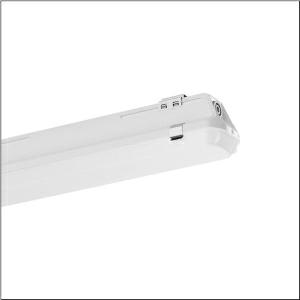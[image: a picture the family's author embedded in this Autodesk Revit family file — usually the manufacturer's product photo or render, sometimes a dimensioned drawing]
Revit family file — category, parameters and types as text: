
# Revit family: monsun_r__21_emergency_51fb107p487b3g_e760
name_source: partatom
category: Lighting Fixtures
units: mm (PartAtom-declared; Revit-internal decimal feet)

## family parameters
Cut with Voids When Loaded = No
Host = Face
Light Source = No
Part Type = Normal
Room Calculation Point = No
Round Connector Dimension = Use Diameter
Shared = No

## types (1)
- Monsun® 21 emergency (1 x LED, 8090 lm, 57.3 W, 4000K)
    Apparent Load = 57 VA
    CIE Flux Codes = 47 77 93 94 100
    Color Rendering = 80
    Color Temperature = 4000K
    Default Elevation = 1800 mm
    Description = Monsun® 21 emergency, damp-proof luminaire, chain hanger, primary optical cover: enclosure, of PMMA, light emission: direct distribution, primary light characteristic: symmetric, installation type: vertical mounting, horizontal mounting, surface-mounted, suspended mounting, LED, rated luminous flux: 8.090lm, luminous efficacy: 141lm/W, light colour: 840, colour temperature: 4000K, control gear: ECG, with terminal, 4-pole, max. 2.5mm², mains connection: 220..240V, AC, 50/60Hz, rated input power: 57W, control gear: single battery element, battery: NiCd, 4,5Ah, mains connection: 230V, housing, of glass-fibre reinforced polyester, uncoated, bright grey, incl. chain hanger, length: 1.590mm, width: 90mm, height: 88mm, clip for enclosure, of stainless steel (V2A), ceiling mounting element, of stainless steel (V2A), chain hanger, of stainless steel (V2A), protection rating (complete): IP66, insulation class (complete): insulation class I (protective earthing), certification: CE, UKCA, protection symbol: D, impact resistance: IK04, permissible operating ambient temperature: +5..+25°C, standard: EN 60598-2-1, EN 50419, EN 60598-2-22, corresponds to IFS (International Featured Standards) requirements for safety and quality in the food industry, for indoor or canopied outdoor use, no direct snow, no direct sun, no direct rain, contact your sales advisor before using the luminaires in applications with unclear chemical exposure, large temperature fluctuations or condensation-forming humidity, LABS conformity tested according to VDMA 24364:2018-05, packaging unit: 1 piece
    Height = 89 mm
    Lamp = 1 x LED
    Lamp Light Flux = 8090 lm
    Lamp Power = 57.3 W
    Lamp count = 1
    Length = 1590 mm
    Luminous efficacy = 141 lm/W
    Manufacturer = Siteco
    ModVariant = No
    Model = 51FB107P487B3G
    Mounting Place = Ceiling
    Mounting Type = Surface mounted
    Number of Poles = 1
    OnlyDefault = Yes
    Power Factor = 1
    Product Name = Monsun® 21 emergency
    Product group = damp-proof luminaire
    ProductGroupID = 300
    Protection Class = Protection class I
    Protection Degree = IP 66
    RLX_Detail_Level = 1
    RLX_Emergency_Light_Flux = 0 lm
    RLX_Emergency_Type = 0
    RLX_Emergency_Type_DB = No
    RlxData = <blob elided: 88901 chars, md5=4cba9751>
    Socket = socket
    Standby Power = 0 W
    System Light Flux = 8090 lm
    System Power = 57 W
    Type Comments = Product without accessories
    Type Image = l_1006717.jpg
    URL = http://relux.com
    VarID = ---
    Voltage = 0 V
    Weight = 0.00 kg
    Width = 90 mm

## geometry (parser evidence)
native form markers: Blend x4, Sweep x11
no freeform markers — native parametric forms only
